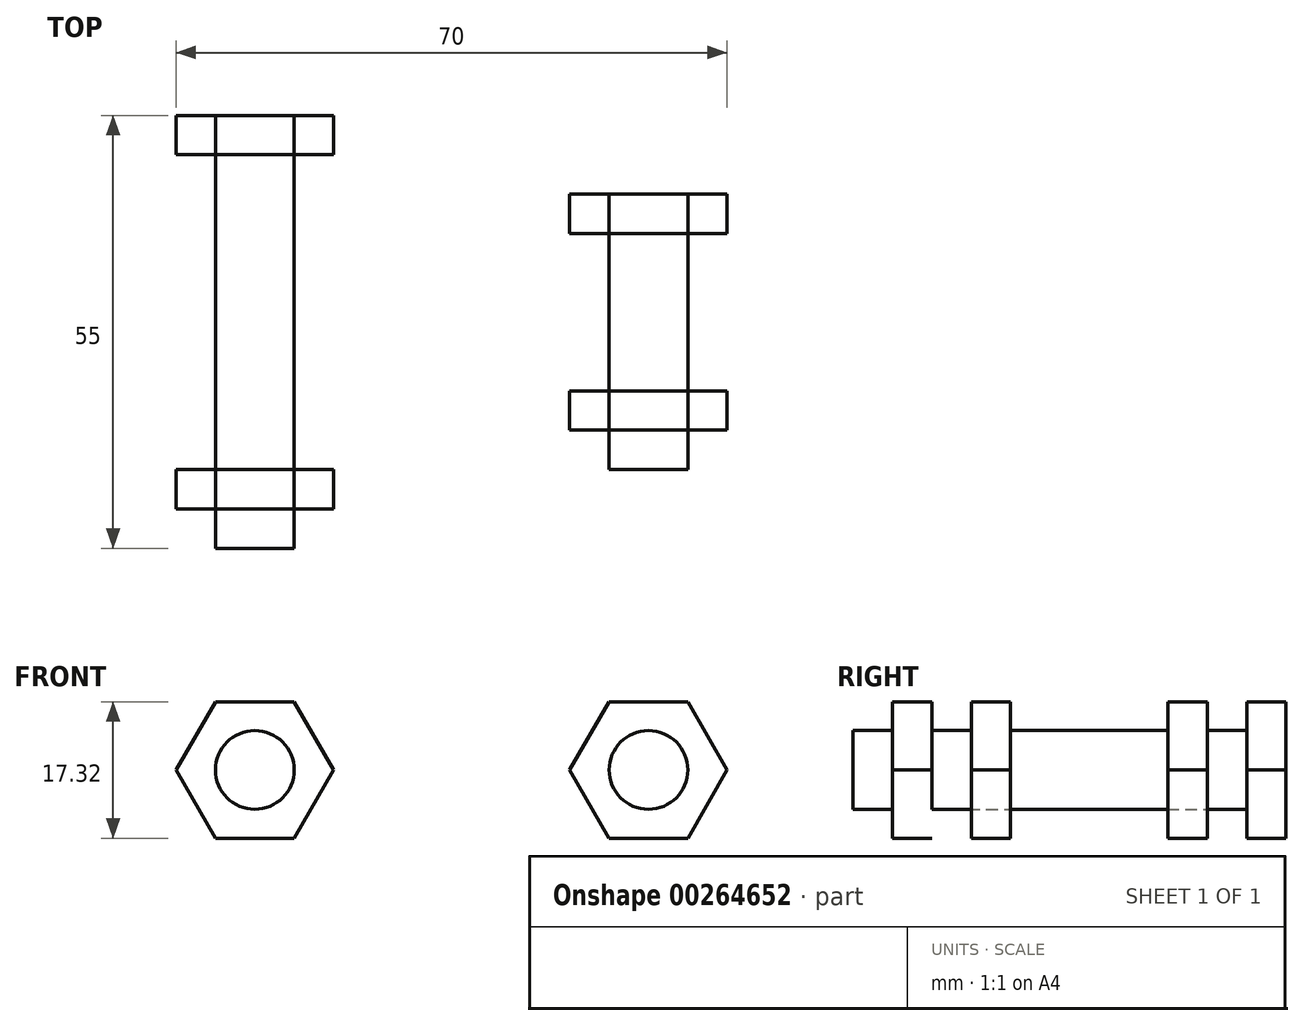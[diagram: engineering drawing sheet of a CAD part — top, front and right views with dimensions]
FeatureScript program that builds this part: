
annotation { "Feature Type Name" : "Feature", "Feature Type Description" : "" }
export const myFeature = defineFeature(function(context is Context, id is Id, definition is map)
    precondition{}
    {
        {
            var Q0;
            Q0=qCreatedBy(makeId("Front.planeOp"),FACE);
            var sketch = newSketch(context, id + "F0", { "sketchPlane" : qUnion([Q0])});
            skCircle(sketch, "E0", {"center": v(0, 0) * mm, "radius": 5 * mm});
            skCircle(sketch, "E1", {"center": v(50, 0) * mm, "radius": 5 * mm});
            skCircle(sketch, "E2.cCircle", {"center": v(0, 0) * mm, "radius": 8.66 * mm, "construction": true});
            skLineSegment(sketch, "E2.0", {"start": v(-5, 8.66) * mm, "end": v(5, 8.66) * mm});
            skLineSegment(sketch, "E2.1", {"start": v(5, 8.66) * mm, "end": v(10, 0) * mm});
            skLineSegment(sketch, "E2.2", {"start": v(10, 0) * mm, "end": v(5, -8.66) * mm});
            skLineSegment(sketch, "E2.3", {"start": v(5, -8.66) * mm, "end": v(-5, -8.66) * mm});
            skLineSegment(sketch, "E2.4", {"start": v(-5, -8.66) * mm, "end": v(-10, 0) * mm});
            skLineSegment(sketch, "E2.5", {"start": v(-10, 0) * mm, "end": v(-5, 8.66) * mm});
            skPoint(sketch, "E2.0.midPoint", {"position": v(0, 8.66) * mm});
            skCircle(sketch, "E3.cCircle", {"center": v(50, 0) * mm, "radius": 8.66 * mm, "construction": true});
            skLineSegment(sketch, "E3.0", {"start": v(45, 8.66) * mm, "end": v(55, 8.66) * mm});
            skLineSegment(sketch, "E3.1", {"start": v(55, 8.66) * mm, "end": v(60, 0) * mm});
            skLineSegment(sketch, "E3.2", {"start": v(60, 0) * mm, "end": v(55, -8.66) * mm});
            skLineSegment(sketch, "E3.3", {"start": v(55, -8.66) * mm, "end": v(45, -8.66) * mm});
            skLineSegment(sketch, "E3.4", {"start": v(45, -8.66) * mm, "end": v(40, 0) * mm});
            skLineSegment(sketch, "E3.5", {"start": v(40, 0) * mm, "end": v(45, 8.66) * mm});
            skPoint(sketch, "E3.0.midPoint", {"position": v(50, 8.66) * mm});
            skSolve(sketch);
        }
        {
            var Q0;
            Q0=makeQuery(id+"F0.imprint","IMPRINT",FACE,{"disambiguationData":[TD([[makeQuery(id+"F0.imprint","IMPRINT",EDGE,{"derivedFrom":sQuery(id+"F0.wireOp",EDGE,"E0")}),1.0]])]});
            extrude(context, id + "F1", {"entities" : qUnion([Q0]), "depth" : 30 * mm, "hasSecondDirection" : true, "secondDirectionOppositeDirection" : true, "secondDirectionDepth" : 25 * mm});
        }
        {
            var Q0;
            Q0=makeQuery(id+"F0.imprint","IMPRINT",FACE,{"disambiguationData":[TD([[makeQuery(id+"F0.imprint","IMPRINT",EDGE,{"derivedFrom":sQuery(id+"F0.wireOp",EDGE,"E0")}),-1.0]])]});
            extrude(context, id + "F2", {"entities" : qUnion([Q0]), "operationType" : NewBodyOperationType.ADD, "endBound" : BoundingType.SYMMETRIC, "depth" : 50 * mm});
        }
        {
            var Q0;
            Q0=makeQuery(id+"F0.imprint","IMPRINT",FACE,{"disambiguationData":[TD([[makeQuery(id+"F0.imprint","IMPRINT",EDGE,{"derivedFrom":sQuery(id+"F0.wireOp",EDGE,"E0")}),-1.0]])]});
            extrude(context, id + "F3", {"entities" : qUnion([Q0]), "operationType" : NewBodyOperationType.REMOVE, "endBound" : BoundingType.SYMMETRIC, "depth" : 40 * mm});
        }
        {
            var Q0;
            Q0=makeQuery(id+"F0.imprint","IMPRINT",FACE,{"disambiguationData":[TD([[makeQuery(id+"F0.imprint","IMPRINT",EDGE,{"derivedFrom":sQuery(id+"F0.wireOp",EDGE,"E1")}),1.0]])]});
            extrude(context, id + "F4", {"entities" : qUnion([Q0]), "depth" : 20 * mm, "hasSecondDirection" : true, "secondDirectionOppositeDirection" : true, "secondDirectionDepth" : 15 * mm});
        }
        {
            var Q0;
            Q0=makeQuery(id+"F0.imprint","IMPRINT",FACE,{"disambiguationData":[TD([[makeQuery(id+"F0.imprint","IMPRINT",EDGE,{"derivedFrom":sQuery(id+"F0.wireOp",EDGE,"E1")}),-1.0]])]});
            extrude(context, id + "F5", {"entities" : qUnion([Q0]), "operationType" : NewBodyOperationType.ADD, "endBound" : BoundingType.SYMMETRIC, "depth" : 30 * mm});
        }
        {
            var Q0;
            Q0=makeQuery(id+"F0.imprint","IMPRINT",FACE,{"disambiguationData":[TD([[makeQuery(id+"F0.imprint","IMPRINT",EDGE,{"derivedFrom":sQuery(id+"F0.wireOp",EDGE,"E1")}),-1.0]])]});
            extrude(context, id + "F6", {"entities" : qUnion([Q0]), "operationType" : NewBodyOperationType.REMOVE, "endBound" : BoundingType.SYMMETRIC, "oppositeDirection" : true, "depth" : 20 * mm});
        }
    });
